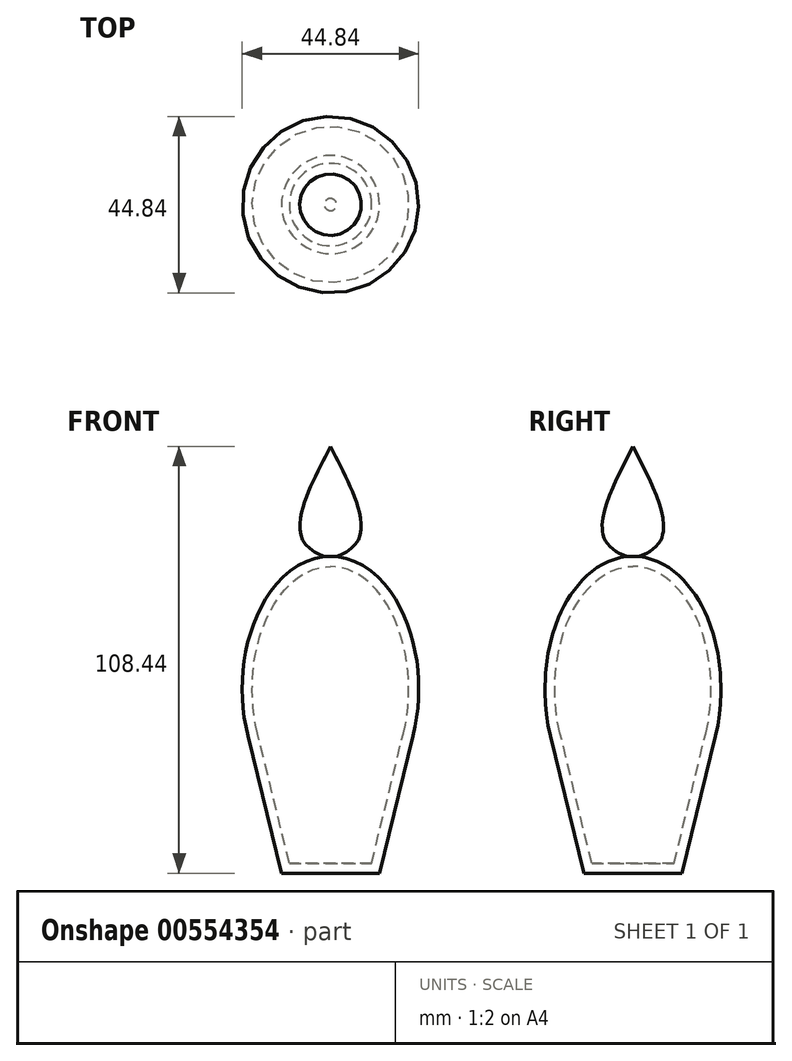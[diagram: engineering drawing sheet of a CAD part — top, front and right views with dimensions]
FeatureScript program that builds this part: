
annotation { "Feature Type Name" : "Feature", "Feature Type Description" : "" }
export const myFeature = defineFeature(function(context is Context, id is Id, definition is map)
    precondition{}
    {
        {
            var Q0;
            Q0=qCreatedBy(makeId("Front.planeOp"),FACE);
            var sketch = newSketch(context, id + "F0", { "sketchPlane" : qUnion([Q0])});
            skEllipticalArc(sketch, "E0", {});
            skLineSegment(sketch, "E1", {"start": v(-21.13, -11.25) * mm, "end": v(-12.46, -46.82) * mm});
            skLineSegment(sketch, "E2", {"start": v(-12.46, -46.82) * mm, "end": v(0, -46.82) * mm});
            skLineSegment(sketch, "E3", {"start": v(0, 33.68) * mm, "end": v(0, -46.82) * mm});
            skPoint(sketch, "E3.endSnap0", {"position": v(0, -33.68) * mm});
            const initialGuessF0  = {"E0": [0, 0, 0, 1, 0.03367584943771362, 0.02241972253017936, 0, 3.141592653589793]};
            skSetInitialGuess(sketch, initialGuessF0);
            skSolve(sketch);
        }
        {
            var Q0;
            {var subQ5=sQuery(id+"F0.wireOp",EDGE,"E2");Q0=makeQuery(id+"F0.imprint","IMPRINT",FACE,{"disambiguationData":[TD([[makeQuery(id+"F0.imprint","IMPRINT",EDGE,{"derivedFrom":subQ5}),1.0]])]});}
            var Q1;
            {var subQ0=sQuery(id+"F0.wireOp",EDGE,"E3");var subQ1=sQuery(id+"F0.wireOp",EDGE,"E0");var subQ2=makeQuery(id+"F0.imprint","INTERSECT",VERTEX,{"disambiguationData":[OD(0.0)],"derivedFrom":[subQ1,subQ0]});Q1=makeQuery(id+"F0.imprint","IMPRINT",FACE,{"disambiguationData":[TD([[makeQuery(id+"F0.imprint","IMPRINT",EDGE,{"disambiguationData":[TD([[subQ2,-1.0]])],"derivedFrom":subQ1}),1.0]])]});}
            var Q2;
            {var subQ0=sQuery(id+"F0.wireOp",EDGE,"E1");var subQ1=sQuery(id+"F0.wireOp",EDGE,"E0");var subQ2=makeQuery(id+"F0.imprint","INTERSECT",VERTEX,{"disambiguationData":[OD(0.0)],"derivedFrom":[subQ1,subQ0]});Q2=makeQuery(id+"F0.imprint","IMPRINT",FACE,{"disambiguationData":[TD([[makeQuery(id+"F0.imprint","IMPRINT",EDGE,{"disambiguationData":[TD([[subQ2,-1.0]])],"derivedFrom":subQ1}),1.0]])]});}
            var Q3;
            Q3=sQuery(id+"F0.wireOp",EDGE,"E3");
            revolve(context, id + "F1", {"entities" : qUnion([Q0, Q1, Q2]), "axis" : qUnion([Q3]), "revolveType" : RevolveType.FULL});
        }
        {
            var Q0;
            Q0=qCreatedBy(makeId("Front.planeOp"),FACE);
            var sketch = newSketch(context, id + "F2", { "sketchPlane" : qUnion([Q0])});
            skFitSpline(sketch, "E4", {"points": [v(0, 61.62) * mm, v(-7.64, 43.47) * mm, v(-6.2, 36.54) * mm, v(0, 32.96) * mm], "startDerivative": vector(-22.66, -43.73) * mm, "endDerivative": vector(26.16, -10.54) * mm});
            skLineSegment(sketch, "E5", {"start": v(0, 32.96) * mm, "end": v(0, 61.62) * mm});
            skSolve(sketch);
        }
        {
            var Q0;
            Q0=qCreatedBy(makeId("Front.planeOp"),FACE);
            var sketch = newSketch(context, id + "F3", { "sketchPlane" : qUnion([Q0])});
            skLineSegment(sketch, "E6", {"start": v(0, 66.64) * mm, "end": v(0, -59.7) * mm});
            skSolve(sketch);
        }
        {
            var Q0;
            Q0=makeQuery(id+"F2.imprint","IMPRINT",FACE,{"disambiguationData":[TD([[makeQuery(id+"F2.imprint","IMPRINT",EDGE,{"derivedFrom":sQuery(id+"F2.wireOp",EDGE,"E4")}),1.0]])]});
            var Q1;
            Q1=sQuery(id+"F3.wireOp",EDGE,"E6");
            revolve(context, id + "F4", {"operationType" : NewBodyOperationType.ADD, "entities" : qUnion([Q0]), "axis" : qUnion([Q1]), "revolveType" : RevolveType.FULL});
        }
        {
            var Q0;
            Q0=makeQuery(id+"F1.opRevolve","SWEPT_FACE",FACE,{"disambiguationData":[OSD([sQuery(id+"F0.wireOp",EDGE,"E1")])]});
            var Q1;
            Q1=makeQuery(id+"F1.opRevolve","SWEPT_FACE",FACE,{"disambiguationData":[OSD([sQuery(id+"F0.wireOp",EDGE,"E0")])]});
            var Q2;
            Q2=makeQuery(id+"F1.opRevolve","SWEPT_BODY",BODY,{"disambiguationData":[OSD([sQuery(id+"F0.wireOp",EDGE,"E0"),sQuery(id+"F0.wireOp",EDGE,"E1"),sQuery(id+"F0.wireOp",EDGE,"E2"),sQuery(id+"F0.wireOp",EDGE,"E3")])]});
            shell(context, id + "F5", {"isHollow" : true, "entities" : qUnion([Q0, Q1]), "parts" : qUnion([Q2]), "thickness" : 2.54 * mm});
        }
        {
            var Q0;
            Q0=makeQuery(id+"F1.opRevolve","SWEPT_BODY",BODY,{"disambiguationData":[OSD([sQuery(id+"F0.wireOp",EDGE,"E0"),sQuery(id+"F0.wireOp",EDGE,"E1"),sQuery(id+"F0.wireOp",EDGE,"E2"),sQuery(id+"F0.wireOp",EDGE,"E3")])]});
            var Q1;
            Q1=makeQuery(id+"F4.opRevolve","SWEPT_FACE",FACE,{"disambiguationData":[OSD([sQuery(id+"F2.wireOp",EDGE,"E4")])]});
            transform(context, id + "F6", {"entities" : qUnion([Q0]), "transformType" : TransformType.ROTATION, "transformAxis" : qUnion([Q1]), "angle" : 30 * degree, "makeCopy" : false});
        }
    });
